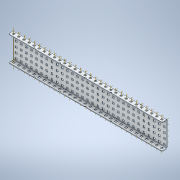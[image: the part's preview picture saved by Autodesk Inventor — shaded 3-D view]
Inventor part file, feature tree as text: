
AUTODESK INVENTOR PART (.ipt)
format: ipt  version: 2020 (Build 240168000, 168)  size: 1,908,736 bytes
history: native  units: in
note: dims shown in document units (in); Inventor stores cm internally (conversion verified against a paired STEP export)
features: other x213, plane x4, pattern_linear x3, split x1, imported_body x1
ambient origin geometry x8: Origin, YZ Plane, XZ Plane, XY Plane, X Axis, Y Axis, Z Axis, Center Point
bodies: Solid1 (feature_tree)
feature tree (222):
  plane  "Work Plane1"
  plane  "Work Plane2"
  plane  "Work Plane3"
  other  "Work Point1"
  other  "Work Point2"
  other  "Work Axis1"
  other  "Work Axis2"
  other  "Work Axis3"
  pattern_linear  "Rectangular Pattern1"  Count1=30 Spacing1=0.5in
  pattern_linear  "Rectangular Pattern2"  Count1=30 Spacing1=0.5in
  pattern_linear  "Rectangular Pattern3"  Count1=30 Spacing1=0.5in
  plane  "Work Plane4"
  split  "Split1"
  other  "Work Point3"
  other  "Work Axis4"
  other  "Work Axis5"
  other  "Work Axis6"
  other  "Work Axis7"
  other  "Work Axis8"
  other  "Work Axis9"
  other  "Work Axis10"
  other  "Work Axis11"
  other  "Work Axis12"
  other  "Work Axis13"
  other  "Work Axis14"
  other  "Work Axis15"
  other  "Work Axis16"
  other  "Work Axis17"
  other  "Work Axis18"
  other  "Work Axis19"
  other  "Work Axis20"
  other  "Work Axis21"
  other  "Work Axis22"
  other  "Work Axis23"
  other  "Work Axis24"
  other  "Work Axis25"
  other  "Work Axis26"
  other  "Work Axis27"
  other  "Work Axis28"
  other  "Work Axis29"
  other  "Work Axis30"
  other  "Work Axis31"
  other  "Work Axis32"
  other  "Work Axis38"
  other  "Work Axis39"
  other  "Work Axis40"
  other  "Work Axis41"
  other  "Work Axis42"
  other  "Work Axis43"
  other  "Work Axis44"
  other  "Work Axis45"
  other  "Work Axis46"
  other  "Work Axis47"
  other  "Work Axis48"
  other  "Work Axis49"
  other  "Work Axis50"
  other  "Work Axis51"
  other  "Work Axis52"
  other  "Work Axis53"
  other  "Work Axis54"
  other  "Work Axis55"
  other  "Work Axis56"
  other  "Work Axis57"
  other  "Work Axis58"
  other  "Work Axis59"
  other  "Work Axis60"
  other  "Work Axis61"
  other  "Work Axis62"
  other  "Work Axis63"
  other  "Work Axis64"
  other  "Work Axis65"
  other  "Work Axis66"
  other  "Work Axis67"
  other  "Work Axis73"
  other  "Work Axis74"
  other  "Work Axis75"
  other  "Work Axis76"
  other  "Work Axis77"
  other  "Work Axis78"
  other  "Work Axis79"
  other  "Work Axis80"
  other  "Work Axis81"
  other  "Work Axis82"
  other  "Work Axis83"
  other  "Work Axis84"
  other  "Work Axis85"
  other  "Work Axis86"
  other  "Work Axis87"
  other  "Work Axis88"
  other  "Work Axis89"
  other  "Work Axis90"
  other  "Work Axis91"
  other  "Work Axis92"
  other  "Work Axis93"
  other  "Work Axis94"
  other  "Work Axis95"
  other  "Work Axis96"
  other  "Work Axis97"
  other  "Work Axis98"
  other  "Work Axis99"
  other  "Work Axis100"
  other  "Work Axis101"
  other  "Work Axis102"
  other  "Work Axis108"
  other  "Work Axis109"
  other  "Work Axis110"
  other  "Work Axis111"
  other  "Work Axis112"
  other  "Work Axis113"
  other  "Work Axis114"
  other  "Work Axis115"
  other  "Work Axis116"
  other  "Work Axis117"
  other  "Work Axis118"
  other  "Work Axis119"
  other  "Work Axis120"
  other  "Work Axis121"
  other  "Work Axis122"
  other  "Work Axis123"
  other  "Work Axis124"
  other  "Work Axis125"
  other  "Work Axis126"
  other  "Work Axis127"
  other  "Work Axis128"
  other  "Work Axis129"
  other  "Work Axis130"
  other  "Work Axis131"
  other  "Work Axis132"
  other  "Work Axis133"
  other  "Work Axis134"
  other  "Work Axis135"
  other  "Work Axis136"
  other  "Work Axis137"
  other  "Work Axis143"
  other  "Work Axis144"
  other  "Work Axis145"
  other  "Work Axis146"
  other  "Work Axis147"
  other  "Work Axis148"
  other  "Work Axis149"
  other  "Work Axis150"
  other  "Work Axis151"
  other  "Work Axis152"
  other  "Work Axis153"
  other  "Work Axis154"
  other  "Work Axis155"
  other  "Work Axis156"
  other  "Work Axis157"
  other  "Work Axis158"
  other  "Work Axis159"
  other  "Work Axis160"
  other  "Work Axis161"
  other  "Work Axis162"
  other  "Work Axis163"
  other  "Work Axis164"
  other  "Work Axis165"
  other  "Work Axis166"
  other  "Work Axis167"
  other  "Work Axis168"
  other  "Work Axis169"
  other  "Work Axis170"
  other  "Work Axis171"
  other  "Work Axis172"
  other  "Work Axis178"
  other  "Work Axis179"
  other  "Work Axis180"
  other  "Work Axis181"
  other  "Work Axis182"
  other  "Work Axis183"
  other  "Work Axis184"
  other  "Work Axis185"
  other  "Work Axis186"
  other  "Work Axis187"
  other  "Work Axis188"
  other  "Work Axis189"
  other  "Work Axis190"
  other  "Work Axis191"
  other  "Work Axis192"
  other  "Work Axis193"
  other  "Work Axis194"
  other  "Work Axis195"
  other  "Work Axis196"
  other  "Work Axis197"
  other  "Work Axis198"
  other  "Work Axis199"
  other  "Work Axis200"
  other  "Work Axis201"
  other  "Work Axis202"
  other  "Work Axis203"
  other  "Work Axis204"
  other  "Work Axis205"
  other  "Work Axis206"
  other  "Work Axis212"
  other  "Work Axis213"
  other  "Work Axis214"
  other  "Work Axis215"
  other  "Work Axis216"
  other  "Work Axis217"
  other  "Work Axis218"
  other  "Work Axis219"
  other  "Work Axis220"
  other  "Work Axis221"
  other  "Work Axis222"
  other  "Work Axis223"
  other  "Work Axis224"
  other  "Work Axis225"
  other  "Work Axis226"
  other  "Work Axis227"
  other  "Work Axis228"
  other  "Work Axis229"
  other  "Work Axis230"
  other  "Work Axis231"
  other  "Work Axis232"
  other  "Work Axis233"
  other  "Work Axis234"
  other  "Work Axis235"
  other  "Work Axis236"
  other  "Work Axis237"
  other  "Work Axis238"
  other  "Work Axis239"
  other  "Work Axis240"
  imported_body  "Imported1"
